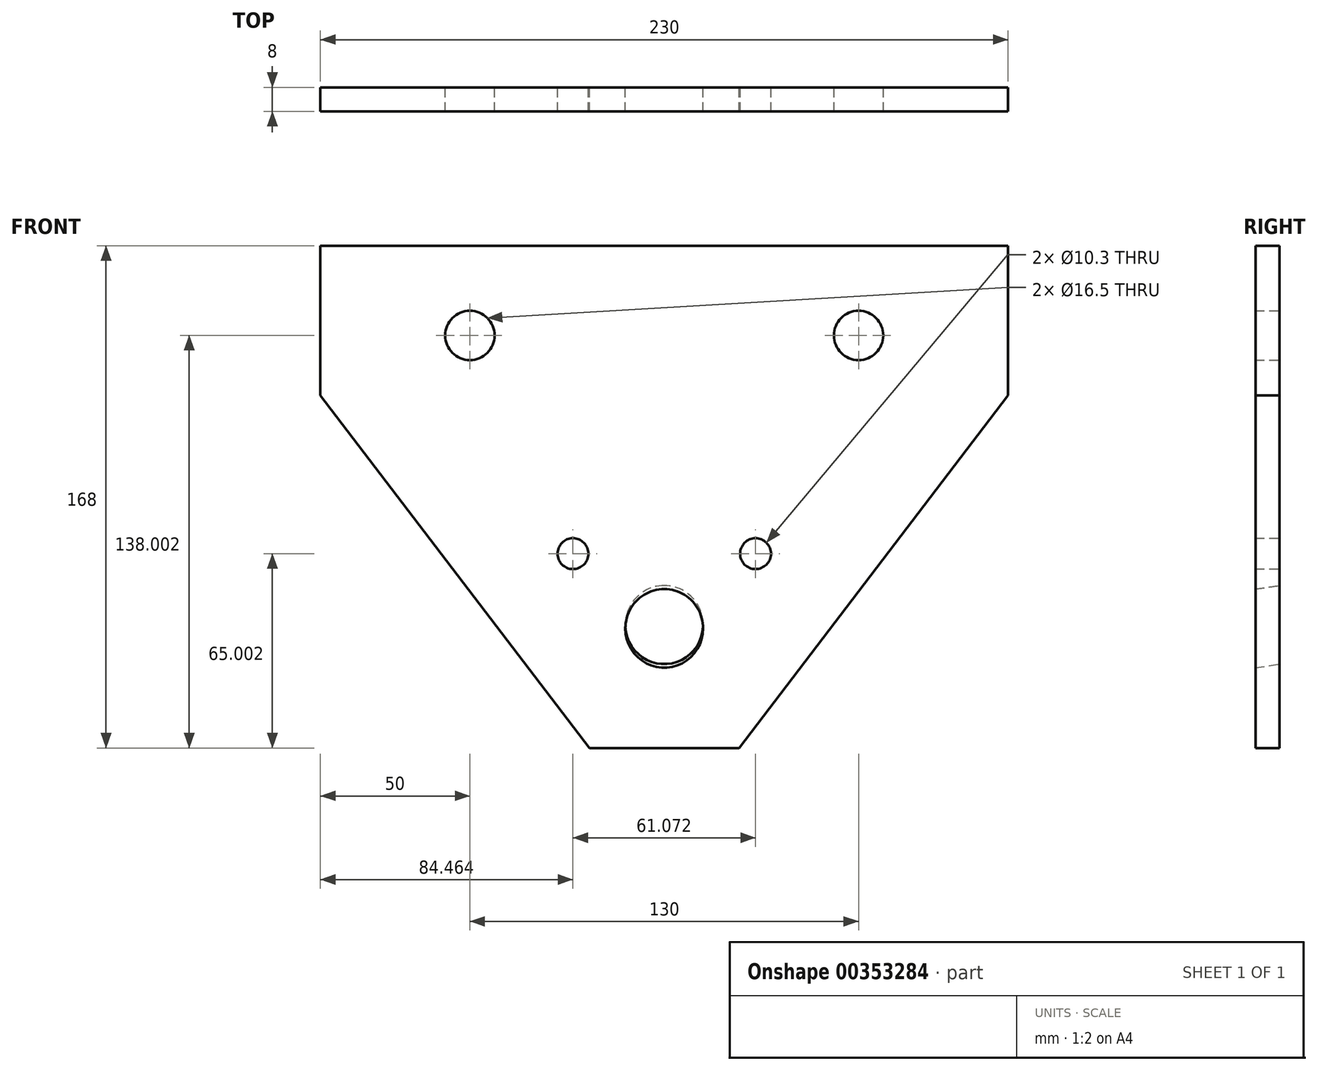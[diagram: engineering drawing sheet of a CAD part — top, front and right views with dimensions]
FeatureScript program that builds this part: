
annotation { "Feature Type Name" : "Feature", "Feature Type Description" : "" }
export const myFeature = defineFeature(function(context is Context, id is Id, definition is map)
    precondition{}
    {
        {
            var Q0;
            Q0=qCreatedBy(makeId("Front.planeOp"),FACE);
            var sketch = newSketch(context, id + "F0", { "sketchPlane" : qUnion([Q0])});
            skLineSegment(sketch, "E0", {"start": v(0, 67.62) * mm, "end": v(-115, 67.62) * mm});
            skLineSegment(sketch, "E1", {"start": v(-115, 67.62) * mm, "end": v(-115, 17.62) * mm});
            skLineSegment(sketch, "E2", {"start": v(-115, 17.62) * mm, "end": v(-25, -100.38) * mm});
            skLineSegment(sketch, "E3", {"start": v(-25, -100.38) * mm, "end": v(0, -100.38) * mm});
            skLineSegment(sketch, "E4.MirrorCS", {"start": v(0, 67.62) * mm, "end": v(115, 67.62) * mm});
            skLineSegment(sketch, "E5.MirrorCS", {"start": v(115, 67.62) * mm, "end": v(115, 17.62) * mm});
            skLineSegment(sketch, "E6.MirrorCS", {"start": v(115, 17.62) * mm, "end": v(25, -100.38) * mm});
            skLineSegment(sketch, "E7.MirrorCS", {"start": v(25, -100.38) * mm, "end": v(0, -100.38) * mm});
            skCircle(sketch, "E8", {"center": v(-65, 37.62) * mm, "radius": 8.25 * mm});
            skCircle(sketch, "E9.MirrorC", {"center": v(65, 37.62) * mm, "radius": 8.25 * mm});
            skLineSegment(sketch, "E10", {"start": v(-115, 37.62) * mm, "end": v(115, 37.62) * mm});
            skCircle(sketch, "E11", {"center": v(-30.54, -35.38) * mm, "radius": 5.15 * mm});
            skCircle(sketch, "E12.MirrorC", {"center": v(30.54, -35.38) * mm, "radius": 5.15 * mm});
            skCircle(sketch, "E13", {"center": v(0, -59.93) * mm, "radius": 13 * mm});
            skLineSegment(sketch, "E14", {"start": v(0, -59.93) * mm, "end": v(13, -59.93) * mm, "construction": true});
            skLineSegment(sketch, "E15", {"start": v(13, -59.93) * mm, "end": v(-13, -59.93) * mm, "construction": true});
            skSolve(sketch);
        }
        {
            var Q0;
            Q0 = qSketchRegion(id + "F0", true);
            var Q1;
            Q1=makeQuery(id+"F0.imprint","IMPRINT",FACE,{"disambiguationData":[TD([[makeQuery(id+"F0.imprint","IMPRINT",EDGE,{"derivedFrom":sQuery(id+"F0.wireOp",EDGE,"E13")}),1.0]])]});
            extrude(context, id + "F1", {"entities" : qUnion([Q0, Q1]), "depth" : 8 * mm});
        }
        {
            var Q0;
            Q0=sQuery(id+"F0.wireOp",EDGE,"E15");
            cPlane(context, id + "F2", {"entities" : qUnion([Q0]), "cplaneType" : CPlaneType.LINE_ANGLE, "offset" : 25 * mm, "angle" : 8.5 * degree, "oppositeDirection" : true, "width" : 150 * mm, "height" : 150 * mm});
        }
        {
            var Q0;
            Q0=qCreatedBy(id+"F2.planeOp",FACE);
            var sketch = newSketch(context, id + "F3", { "sketchPlane" : qUnion([Q0])});
            skCircle(sketch, "E16", {"center": v(0, -58.52) * mm, "radius": 13 * mm});
            skSolve(sketch);
        }
        {
            var Q0;
            Q0 = qSketchRegion(id + "F3", true);
            extrude(context, id + "F4", {"entities" : qUnion([Q0]), "operationType" : NewBodyOperationType.REMOVE, "depth" : 230 * mm});
        }
        {
            var Q0;
            Q0 = qSketchRegion(id + "F3", true);
            extrude(context, id + "F5", {"entities" : qUnion([Q0]), "operationType" : NewBodyOperationType.REMOVE, "oppositeDirection" : true, "depth" : 25 * mm});
        }
    });
